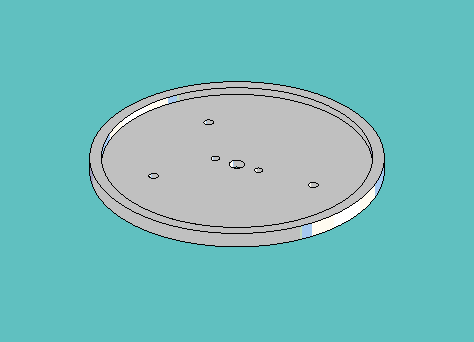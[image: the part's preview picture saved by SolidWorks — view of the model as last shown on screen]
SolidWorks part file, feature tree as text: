
SOLIDWORKS PART (.sldprt)
format: sldprt  version: not decoded by parser v0  size: 226,304 bytes
history: native  units: mm
features: sketch x4, extrude x3, material x1, cut_extrude x1 (+11 scaffold rows collapsed)
feature tree (20):
  scaffold x11  (default folders/planes/origin — collapsed)
  material  "Material <not specified>"
  sketch  "Sketch1"  dims[D1=119.38mm D2=6.35mm]
  extrude  "Extrude1"  Depth=3.175mm
  sketch  "Sketch2"  dims[D1=109.855mm]
  extrude  "Extrude2"  Depth=3.175mm
  sketch  "Sketch3"  dims[c1.D1=69.85mm c1.D4=~3.96875mm c1.D5=~3.96875mm c1.D6=~3.96875mm c1.D7=~19.84375mm c1.D8=3.4544mm c1.D9=3.4544mm c1.D2=~151.871657mm c2.D2=43.0deg c2.D3=~74.030283mm c3.D3=43.0deg]
  cut_extrude  "Cut-Extrude1"  [1 undecoded]
  sketch  "Sketch4"  dims[D1=12.7mm]
  extrude  "Extrude3"  Depth=6.35mm
decode coverage: 7 of 8 modeling features carry decoded parameters
note: ~ marks probable driven/reference dimensions
note: 1 parameter value undecoded
note: suppression state not decoded; provenance and decode notes live in map.json
